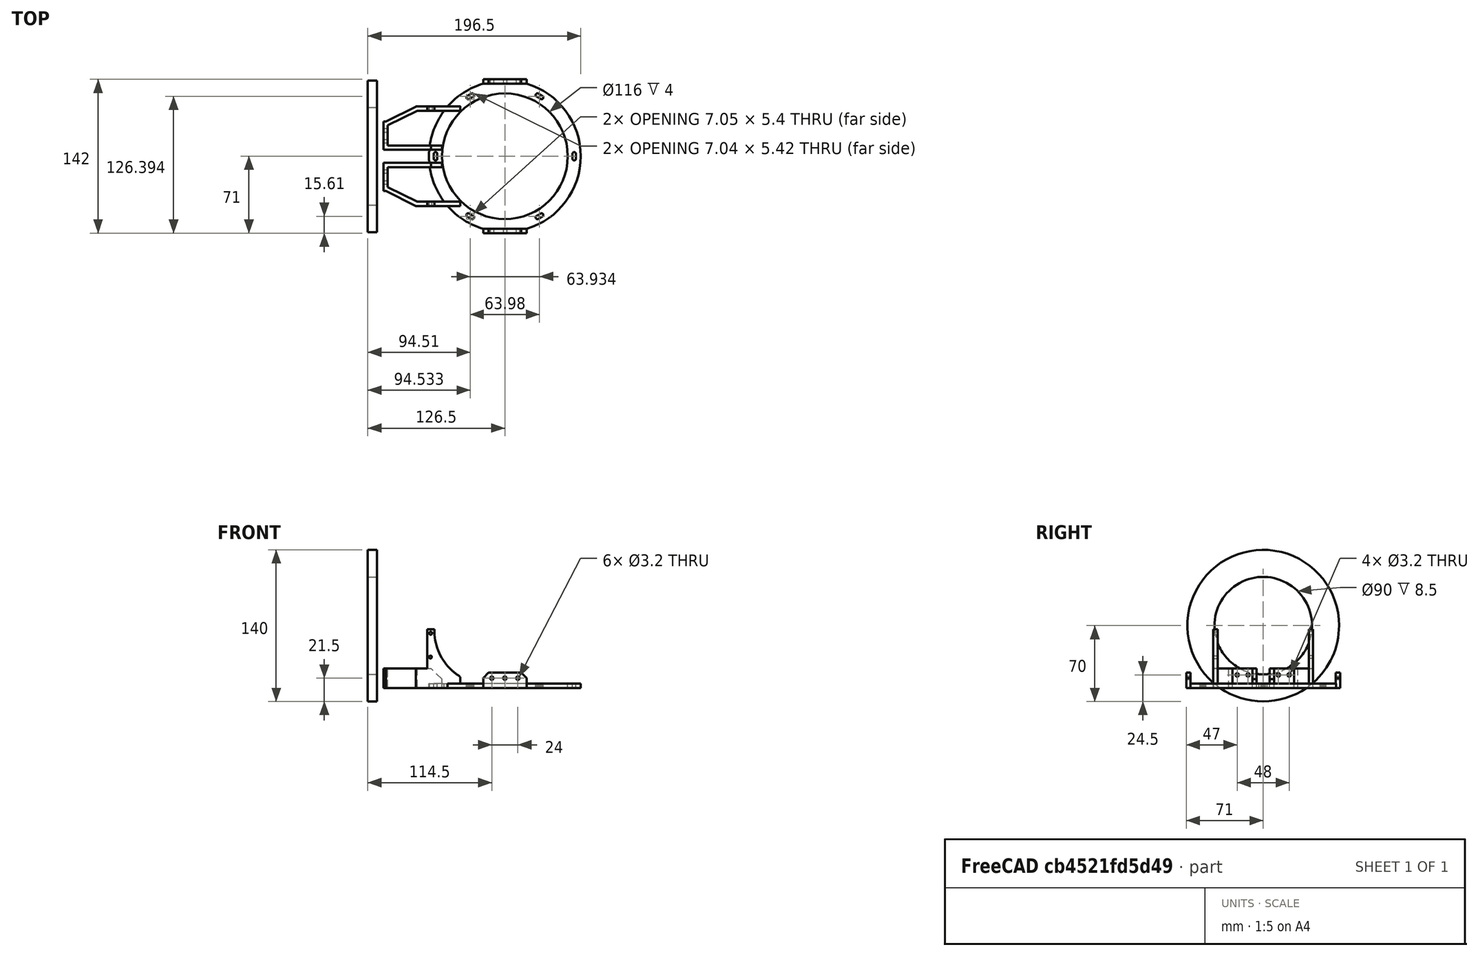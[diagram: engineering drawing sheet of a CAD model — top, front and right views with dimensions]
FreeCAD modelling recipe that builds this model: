
FCSTD DOCUMENT  (FreeCAD 0.15R4671 (Git))
Label: back_roll_plate
License: All rights reserved
LicenseURL: http://en.wikipedia.org/wiki/All_rights_reserved
objects: Part::Cylinder×65, Part::MultiFuse×35, Part::Box×13, Part::Cut×5, Part::Chamfer×4, Part::Mirroring×2, Part::Fillet×1
note: 125 computed .brp shape members not serialized (recipe doc carries the construction recipe); baked Part::Feature solids carry a one-line shape summary decoded from their .brp

FEATURE [Part::Cylinder] Cylinder
  Angle = 360
  Height = 4
  Radius = 70
FEATURE [Part::Cylinder] Cylinder001
  Angle = 360
  Height = 10
  Placement = pos=(0,0,-3) rot=(0,0,1;0rad)
  Radius = 58
FEATURE [Part::Cut] Cut
  Base = -> Cylinder
  Tool = -> Cylinder001
FEATURE [Part::Box] Box  label="Cube"
  Height = 14
  Length = 40
  Placement = pos=(-20,67,0) rot=(0,0,1;0rad)
  Width = 4
FEATURE [Part::Box] Box001  label="Cube001"
  Height = 3
  Length = 40
  Placement = pos=(-20,60,0) rot=(0,0,1;0rad)
  Width = 10
FEATURE [Part::Box] Box002  label="Cube002"
  Height = 14
  Length = 40
  Placement = pos=(-20,-71,0) rot=(0,0,1;0rad)
  Width = 4
FEATURE [Part::Box] Box003  label="Cube003"
  Height = 3
  Length = 40
  Placement = pos=(-20,-71,0) rot=(0,0,1;0rad)
  Width = 10
FEATURE [Part::Cylinder] Cylinder034
  Angle = 360
  Height = 10
  Placement = pos=(64,0,-2) rot=(0,0,1;0rad)
  Radius = 1.6
FEATURE [Part::Cylinder] Cylinder035
  Angle = 360
  Height = 10
  Placement = pos=(-64,0,-2) rot=(0,0,1;0rad)
  Radius = 1.6
FEATURE [Part::MultiFuse] Fusion018
  Placement = pos=(0,0,0) rot=(0,0,1;0.017453rad)
  Shapes = -> [Cylinder034,Cylinder035]
FEATURE [Part::Cylinder] Cylinder036
  Angle = 360
  Height = 10
  Placement = pos=(64,0,-2) rot=(0,0,1;0rad)
  Radius = 1.6
FEATURE [Part::Cylinder] Cylinder037
  Angle = 360
  Height = 10
  Placement = pos=(-64,0,-2) rot=(0,0,1;0rad)
  Radius = 1.6
FEATURE [Part::MultiFuse] Fusion019
  Placement = pos=(0,0,0) rot=(0,0,1;0.034907rad)
  Shapes = -> [Cylinder036,Cylinder037]
FEATURE [Part::Cylinder] Cylinder038
  Angle = 360
  Height = 10
  Placement = pos=(64,0,-2) rot=(0,0,1;0rad)
  Radius = 1.6
FEATURE [Part::Cylinder] Cylinder039
  Angle = 360
  Height = 10
  Placement = pos=(-64,0,-2) rot=(0,0,1;0rad)
  Radius = 1.6
FEATURE [Part::MultiFuse] Fusion020
  Placement = pos=(0,0,0) rot=(0,0,-1;0.017453rad)
  Shapes = -> [Cylinder038,Cylinder039]
FEATURE [Part::Cylinder] Cylinder040
  Angle = 360
  Height = 10
  Placement = pos=(64,0,-2) rot=(0,0,1;0rad)
  Radius = 1.6
FEATURE [Part::Cylinder] Cylinder041
  Angle = 360
  Height = 10
  Placement = pos=(-64,0,-2) rot=(0,0,1;0rad)
  Radius = 1.6
FEATURE [Part::MultiFuse] Fusion021
  Placement = pos=(0,0,0) rot=(0,0,-1;0.034907rad)
  Shapes = -> [Cylinder040,Cylinder041]
FEATURE [Part::Cylinder] Cylinder042
  Angle = 360
  Height = 10
  Placement = pos=(64,0,-2) rot=(0,0,1;0rad)
  Radius = 1.6
FEATURE [Part::Cylinder] Cylinder043
  Angle = 360
  Height = 10
  Placement = pos=(-64,0,-2) rot=(0,0,1;0rad)
  Radius = 1.6
FEATURE [Part::MultiFuse] Fusion022
  Placement = pos=(0,0,0) rot=(0,0,-1;0.008727rad)
  Shapes = -> [Cylinder042,Cylinder043]
FEATURE [Part::Cylinder] Cylinder044
  Angle = 360
  Height = 10
  Placement = pos=(64,0,-2) rot=(0,0,1;0rad)
  Radius = 1.6
FEATURE [Part::Cylinder] Cylinder045
  Angle = 360
  Height = 10
  Placement = pos=(-64,0,-2) rot=(0,0,1;0rad)
  Radius = 1.6
FEATURE [Part::MultiFuse] Fusion023
  Placement = pos=(0,0,0) rot=(0,0,-1;0.02618rad)
  Shapes = -> [Cylinder044,Cylinder045]
FEATURE [Part::Cylinder] Cylinder046
  Angle = 360
  Height = 10
  Placement = pos=(64,0,-2) rot=(0,0,1;0rad)
  Radius = 1.6
FEATURE [Part::Cylinder] Cylinder047
  Angle = 360
  Height = 10
  Placement = pos=(-64,0,-2) rot=(0,0,1;0rad)
  Radius = 1.6
FEATURE [Part::MultiFuse] Fusion024
  Placement = pos=(0,0,0) rot=(0,0,1;0.02618rad)
  Shapes = -> [Cylinder046,Cylinder047]
FEATURE [Part::Cylinder] Cylinder048
  Angle = 360
  Height = 10
  Placement = pos=(64,0,-2) rot=(0,0,1;0rad)
  Radius = 1.6
FEATURE [Part::Cylinder] Cylinder049
  Angle = 360
  Height = 10
  Placement = pos=(-64,0,-2) rot=(0,0,1;0rad)
  Radius = 1.6
FEATURE [Part::MultiFuse] Fusion025
  Placement = pos=(0,0,0) rot=(0,0,1;0.008727rad)
  Shapes = -> [Cylinder048,Cylinder049]
FEATURE [Part::MultiFuse] Fusion026
  Placement = pos=(0,0,0) rot=(0,0,1;2.0944rad)
  Shapes = -> [Fusion021,Fusion024,Fusion019,Fusion023,Fusion020,Fusion022,Fusion018,Fusion025]
FEATURE [Part::Cylinder] Cylinder050
  Angle = 360
  Height = 10
  Placement = pos=(64,0,-2) rot=(0,0,1;0rad)
  Radius = 1.6
FEATURE [Part::Cylinder] Cylinder051
  Angle = 360
  Height = 10
  Placement = pos=(-64,0,-2) rot=(0,0,1;0rad)
  Radius = 1.6
FEATURE [Part::MultiFuse] Fusion
  Placement = pos=(0,0,0) rot=(0,0,1;0.017453rad)
  Shapes = -> [Cylinder050,Cylinder051]
FEATURE [Part::Cylinder] Cylinder052
  Angle = 360
  Height = 10
  Placement = pos=(64,0,-2) rot=(0,0,1;0rad)
  Radius = 1.6
FEATURE [Part::Cylinder] Cylinder053
  Angle = 360
  Height = 10
  Placement = pos=(-64,0,-2) rot=(0,0,1;0rad)
  Radius = 1.6
FEATURE [Part::MultiFuse] Fusion027
  Placement = pos=(0,0,0) rot=(0,0,1;0.034907rad)
  Shapes = -> [Cylinder052,Cylinder053]
FEATURE [Part::Cylinder] Cylinder054
  Angle = 360
  Height = 10
  Placement = pos=(64,0,-2) rot=(0,0,1;0rad)
  Radius = 1.6
FEATURE [Part::Cylinder] Cylinder055
  Angle = 360
  Height = 10
  Placement = pos=(-64,0,-2) rot=(0,0,1;0rad)
  Radius = 1.6
FEATURE [Part::MultiFuse] Fusion028
  Placement = pos=(0,0,0) rot=(0,0,-1;0.017453rad)
  Shapes = -> [Cylinder054,Cylinder055]
FEATURE [Part::Cylinder] Cylinder056
  Angle = 360
  Height = 10
  Placement = pos=(64,0,-2) rot=(0,0,1;0rad)
  Radius = 1.6
FEATURE [Part::Cylinder] Cylinder057
  Angle = 360
  Height = 10
  Placement = pos=(-64,0,-2) rot=(0,0,1;0rad)
  Radius = 1.6
FEATURE [Part::MultiFuse] Fusion029
  Placement = pos=(0,0,0) rot=(0,0,-1;0.034907rad)
  Shapes = -> [Cylinder056,Cylinder057]
FEATURE [Part::Cylinder] Cylinder058
  Angle = 360
  Height = 10
  Placement = pos=(64,0,-2) rot=(0,0,1;0rad)
  Radius = 1.6
FEATURE [Part::Cylinder] Cylinder059
  Angle = 360
  Height = 10
  Placement = pos=(-64,0,-2) rot=(0,0,1;0rad)
  Radius = 1.6
FEATURE [Part::MultiFuse] Fusion030
  Placement = pos=(0,0,0) rot=(0,0,-1;0.008727rad)
  Shapes = -> [Cylinder058,Cylinder059]
FEATURE [Part::Cylinder] Cylinder060
  Angle = 360
  Height = 10
  Placement = pos=(64,0,-2) rot=(0,0,1;0rad)
  Radius = 1.6
FEATURE [Part::Cylinder] Cylinder061
  Angle = 360
  Height = 10
  Placement = pos=(-64,0,-2) rot=(0,0,1;0rad)
  Radius = 1.6
FEATURE [Part::MultiFuse] Fusion031
  Placement = pos=(0,0,0) rot=(0,0,-1;0.02618rad)
  Shapes = -> [Cylinder060,Cylinder061]
FEATURE [Part::Cylinder] Cylinder062
  Angle = 360
  Height = 10
  Placement = pos=(64,0,-2) rot=(0,0,1;0rad)
  Radius = 1.6
FEATURE [Part::Cylinder] Cylinder063
  Angle = 360
  Height = 10
  Placement = pos=(-64,0,-2) rot=(0,0,1;0rad)
  Radius = 1.6
FEATURE [Part::MultiFuse] Fusion032
  Placement = pos=(0,0,0) rot=(0,0,1;0.02618rad)
  Shapes = -> [Cylinder062,Cylinder063]
FEATURE [Part::Cylinder] Cylinder064
  Angle = 360
  Height = 10
  Placement = pos=(64,0,-2) rot=(0,0,1;0rad)
  Radius = 1.6
FEATURE [Part::Cylinder] Cylinder065
  Angle = 360
  Height = 10
  Placement = pos=(-64,0,-2) rot=(0,0,1;0rad)
  Radius = 1.6
FEATURE [Part::MultiFuse] Fusion033
  Placement = pos=(0,0,0) rot=(0,0,1;0.008727rad)
  Shapes = -> [Cylinder064,Cylinder065]
FEATURE [Part::MultiFuse] Fusion034
  Placement = pos=(0,0,0) rot=(0,0,1;1.0472rad)
  Shapes = -> [Fusion029,Fusion032,Fusion027,Fusion031,Fusion028,Fusion030,Fusion,Fusion033]
FEATURE [Part::Cylinder] Cylinder066
  Angle = 360
  Height = 10
  Placement = pos=(64,0,-2) rot=(0,0,1;0rad)
  Radius = 1.6
FEATURE [Part::Cylinder] Cylinder067
  Angle = 360
  Height = 10
  Placement = pos=(-64,0,-2) rot=(0,0,1;0rad)
  Radius = 1.6
FEATURE [Part::MultiFuse] Fusion035
  Placement = pos=(0,0,0) rot=(0,0,1;0.017453rad)
  Shapes = -> [Cylinder066,Cylinder067]
FEATURE [Part::Cylinder] Cylinder068
  Angle = 360
  Height = 10
  Placement = pos=(64,0,-2) rot=(0,0,1;0rad)
  Radius = 1.6
FEATURE [Part::Cylinder] Cylinder069
  Angle = 360
  Height = 10
  Placement = pos=(-64,0,-2) rot=(0,0,1;0rad)
  Radius = 1.6
FEATURE [Part::MultiFuse] Fusion036
  Placement = pos=(0,0,0) rot=(0,0,1;0.034907rad)
  Shapes = -> [Cylinder068,Cylinder069]
FEATURE [Part::Cylinder] Cylinder070
  Angle = 360
  Height = 10
  Placement = pos=(64,0,-2) rot=(0,0,1;0rad)
  Radius = 1.6
FEATURE [Part::Cylinder] Cylinder071
  Angle = 360
  Height = 10
  Placement = pos=(-64,0,-2) rot=(0,0,1;0rad)
  Radius = 1.6
FEATURE [Part::MultiFuse] Fusion037
  Placement = pos=(0,0,0) rot=(0,0,-1;0.017453rad)
  Shapes = -> [Cylinder070,Cylinder071]
FEATURE [Part::Cylinder] Cylinder072
  Angle = 360
  Height = 10
  Placement = pos=(64,0,-2) rot=(0,0,1;0rad)
  Radius = 1.6
FEATURE [Part::Cylinder] Cylinder073
  Angle = 360
  Height = 10
  Placement = pos=(-64,0,-2) rot=(0,0,1;0rad)
  Radius = 1.6
FEATURE [Part::MultiFuse] Fusion038
  Placement = pos=(0,0,0) rot=(0,0,-1;0.034907rad)
  Shapes = -> [Cylinder072,Cylinder073]
FEATURE [Part::Cylinder] Cylinder074
  Angle = 360
  Height = 10
  Placement = pos=(64,0,-2) rot=(0,0,1;0rad)
  Radius = 1.6
FEATURE [Part::Cylinder] Cylinder075
  Angle = 360
  Height = 10
  Placement = pos=(-64,0,-2) rot=(0,0,1;0rad)
  Radius = 1.6
FEATURE [Part::MultiFuse] Fusion039
  Placement = pos=(0,0,0) rot=(0,0,-1;0.008727rad)
  Shapes = -> [Cylinder074,Cylinder075]
FEATURE [Part::Cylinder] Cylinder076
  Angle = 360
  Height = 10
  Placement = pos=(64,0,-2) rot=(0,0,1;0rad)
  Radius = 1.6
FEATURE [Part::Cylinder] Cylinder077
  Angle = 360
  Height = 10
  Placement = pos=(-64,0,-2) rot=(0,0,1;0rad)
  Radius = 1.6
FEATURE [Part::MultiFuse] Fusion040
  Placement = pos=(0,0,0) rot=(0,0,-1;0.02618rad)
  Shapes = -> [Cylinder076,Cylinder077]
FEATURE [Part::Cylinder] Cylinder078
  Angle = 360
  Height = 10
  Placement = pos=(64,0,-2) rot=(0,0,1;0rad)
  Radius = 1.6
FEATURE [Part::Cylinder] Cylinder079
  Angle = 360
  Height = 10
  Placement = pos=(-64,0,-2) rot=(0,0,1;0rad)
  Radius = 1.6
FEATURE [Part::MultiFuse] Fusion041
  Placement = pos=(0,0,0) rot=(0,0,1;0.02618rad)
  Shapes = -> [Cylinder078,Cylinder079]
FEATURE [Part::Cylinder] Cylinder080
  Angle = 360
  Height = 10
  Placement = pos=(64,0,-2) rot=(0,0,1;0rad)
  Radius = 1.6
FEATURE [Part::Cylinder] Cylinder081
  Angle = 360
  Height = 10
  Placement = pos=(-64,0,-2) rot=(0,0,1;0rad)
  Radius = 1.6
FEATURE [Part::MultiFuse] Fusion042
  Placement = pos=(0,0,0) rot=(0,0,1;0.008727rad)
  Shapes = -> [Cylinder080,Cylinder081]
FEATURE [Part::MultiFuse] Fusion043
  Shapes = -> [Fusion038,Fusion041,Fusion036,Fusion040,Fusion037,Fusion039,Fusion035,Fusion042]
FEATURE [Part::MultiFuse] Fusion044
  Shapes = -> [Fusion026,Fusion043,Fusion034]
FEATURE [Part::Cut] Cut001
  Base = -> Cut
  Tool = -> Fusion044
FEATURE [Part::Box] Box004  label="Cube004"
  Height = 18
  Length = 41
  Placement = pos=(-82,42,0) rot=(0,0,1;0rad)
  Width = 4
FEATURE [Part::Box] Box005  label="Cube005"
  Height = 18
  Length = 41
  Placement = pos=(-82,-46,0) rot=(0,0,1;0rad)
  Width = 4
FEATURE [Part::Box] Box006  label="Cube006"
  Height = 18
  Length = 54
  Placement = pos=(-112,6,0) rot=(0,0,1;0rad)
  Width = 4
FEATURE [Part::Box] Box007  label="Cube007"
  Height = 18
  Length = 54
  Placement = pos=(-112,-10,0) rot=(0,0,1;0rad)
  Width = 4
FEATURE [Part::Box] Box008  label="Cube008"
  Height = 18
  Length = 4
  Placement = pos=(-112,6,0) rot=(0,0,1;0rad)
  Width = 26
FEATURE [Part::Box] Box009  label="Cube009"
  Height = 18
  Length = 4
  Placement = pos=(-112,-32,0) rot=(0,0,1;0rad)
  Width = 26
FEATURE [Part::Box] Box011  label="Cube011"
  Height = 36
  Length = 30.5
  Placement = pos=(-71.5,42,18) rot=(0,0,1;0rad)
  Width = 4
FEATURE [Part::Box] Box012  label="Cube012"
  Height = 36
  Length = 30.5
  Placement = pos=(-71.5,-46,18) rot=(0,0,1;0rad)
  Width = 4
FEATURE [Part::Cylinder] Cylinder082
  Angle = 360
  Height = 10
  Placement = pos=(0,-62,9) rot=(1,0,0;1.5708rad)
  Radius = 1.6
FEATURE [Part::Cylinder] Cylinder083
  Angle = 360
  Height = 10
  Placement = pos=(12,-62,9) rot=(1,0,0;1.5708rad)
  Radius = 1.6
FEATURE [Part::Cylinder] Cylinder084
  Angle = 360
  Height = 10
  Placement = pos=(-12,-62,9) rot=(1,0,0;1.5708rad)
  Radius = 1.6
FEATURE [Part::MultiFuse] Fusion045
  Shapes = -> [Cylinder082,Cylinder083,Cylinder084]
FEATURE [Part::Cylinder] Cylinder085
  Angle = 360
  Height = 10
  Placement = pos=(0,-62,9) rot=(1,0,0;1.5708rad)
  Radius = 1.6
FEATURE [Part::Cylinder] Cylinder086
  Angle = 360
  Height = 10
  Placement = pos=(12,-62,9) rot=(1,0,0;1.5708rad)
  Radius = 1.6
FEATURE [Part::Cylinder] Cylinder087
  Angle = 360
  Height = 10
  Placement = pos=(-12,-62,9) rot=(1,0,0;1.5708rad)
  Radius = 1.6
FEATURE [Part::MultiFuse] Fusion046
  Placement = pos=(0,134,0) rot=(0,0,1;0rad)
  Shapes = -> [Cylinder085,Cylinder086,Cylinder087]
FEATURE [Part::Cylinder] Cylinder088
  Angle = 360
  Height = 8.5
  Placement = pos=(0,107,180) rot=(1,0,0;1.5708rad)
  Radius = 70
FEATURE [Part::Cylinder] Cylinder089
  Angle = 360
  Height = 20
  Placement = pos=(0,111,180) rot=(1,0,0;1.5708rad)
  Radius = 45
FEATURE [Part::Cut] Cut002  label="Cut034"
  Base = -> Cylinder088
  Placement = pos=(-19.5,0,-122.5) rot=(0,0,1;1.5708rad)
  Tool = -> Cylinder089
FEATURE [Part::Box] Box013  label="Cube013"
  Height = 18
  Length = 33.1
  Placement = pos=(-109.75,27.6,0) rot=(0,0,1;0.462512rad)
  Width = 4
FEATURE [Part::Mirroring] Part__Mirroring  label="Cube013 (Mirror #1)"
  Base = (0,0,0)
  Normal = (0,1,0)
  Source = -> Box013
FEATURE [Part::Cylinder] Cylinder090
  Angle = 360
  Height = 10
  Placement = pos=(-106,14,12) rot=(0,1,0;1.5708rad)
  Radius = 1.6
FEATURE [Part::Cylinder] Cylinder091
  Angle = 360
  Height = 10
  Placement = pos=(-106,24,12) rot=(0,1,0;1.5708rad)
  Radius = 1.6
FEATURE [Part::MultiFuse] Fusion047
  Placement = pos=(-10,0,0) rot=(0,0,1;0rad)
  Shapes = -> [Cylinder090,Cylinder091]
FEATURE [Part::Cylinder] Cylinder092
  Angle = 360
  Height = 10
  Placement = pos=(-106,14,12) rot=(0,1,0;1.5708rad)
  Radius = 1.6
FEATURE [Part::Cylinder] Cylinder093
  Angle = 360
  Height = 10
  Placement = pos=(-106,24,12) rot=(0,1,0;1.5708rad)
  Radius = 1.6
FEATURE [Part::MultiFuse] Fusion048
  Placement = pos=(-10,-38,0) rot=(0,0,1;0rad)
  Shapes = -> [Cylinder092,Cylinder093]
FEATURE [Part::Cylinder] Cylinder094
  Angle = 360
  Height = 10
  Placement = pos=(-58.7,50,28.5) rot=(1,0,0;1.5708rad)
  Radius = 1.35
FEATURE [Part::Cylinder] Cylinder095
  Angle = 360
  Height = 10
  Placement = pos=(-58.5,50,50.5) rot=(1,0,0;1.5708rad)
  Radius = 1.35
FEATURE [Part::MultiFuse] Fusion049
  Placement = pos=(-10,0,0) rot=(0,0,1;0rad)
  Shapes = -> [Cylinder094,Cylinder095]
FEATURE [Part::Mirroring] Part__Mirroring001  label="Fusion049 (Mirror #2)"
  Base = (0,0,0)
  Normal = (0,1,0)
  Source = -> Fusion049
FEATURE [Part::MultiFuse] Fusion050
  Shapes = -> [Part__Mirroring001,Fusion048,Fusion047,Fusion049,Fusion045,Fusion046]
FEATURE [Part::Chamfer] Chamfer
  Base = -> Box006
  Edges = 1 edges r=10: [Edge6]
FEATURE [Part::Chamfer] Chamfer001
  Base = -> Box007
  Edges = 1 edges r=10: [Edge6]
FEATURE [Part::Chamfer] Chamfer002
  Base = -> Box002
  Edges = 2 edges r=5: [Edge2,Edge6]
FEATURE [Part::Chamfer] Chamfer003
  Base = -> Box
  Edges = 2 edges r=5: [Edge2,Edge6]
FEATURE [Part::MultiFuse] Fusion051
  Shapes = -> [Box011,Box003,Box012,Box001,Box009,Chamfer,Part__Mirroring,Box004,Cut001,Box008,Chamfer003,Box005,Chamfer002,Chamfer001,Box013]
FEATURE [Part::Cylinder] Cylinder096
  Angle = 360
  Height = 95
  Placement = pos=(-15,47.5,53) rot=(1,0,0;1.5708rad)
  Radius = 50
FEATURE [Part::Cut] Cut003
  Base = -> Fusion051
  Tool = -> Cylinder096
FEATURE [Part::Cut] Cut004
  Base = -> Cut003
  Tool = -> Fusion050
FEATURE [Part::Fillet] Fillet
  Base = -> Cut004
  Edges = 2 edges r=3: [Edge410,Edge459]
